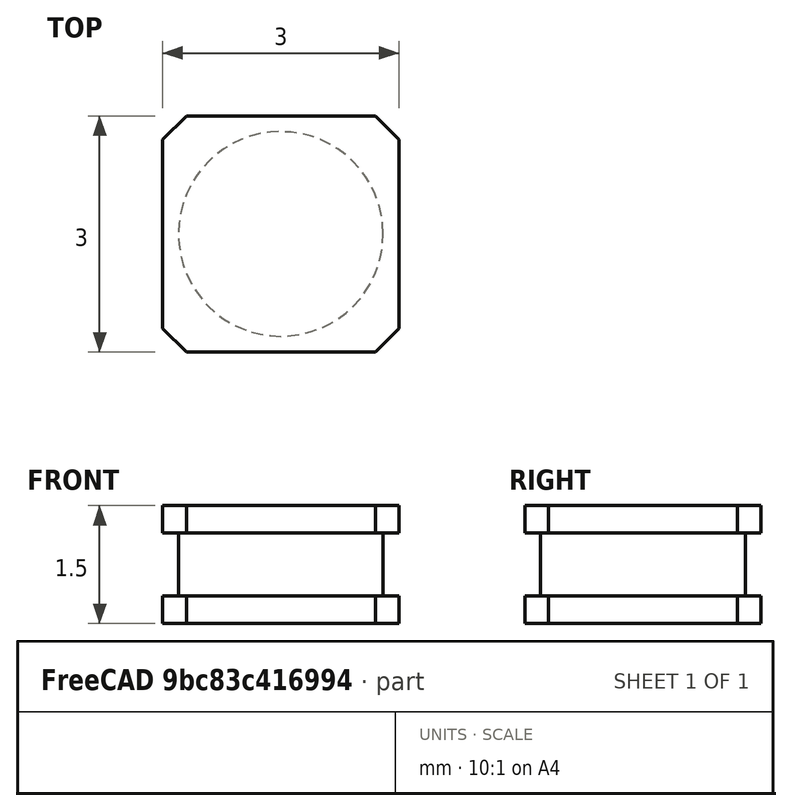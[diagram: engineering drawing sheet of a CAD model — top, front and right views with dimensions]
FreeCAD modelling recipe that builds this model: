
FCSTD DOCUMENT  (FreeCAD 0.19R24366 (Git))
Label: Inductor_shielded_3.0_3.0_1.5
License: All rights reserved
LicenseURL: http://en.wikipedia.org/wiki/All_rights_reserved
objects: Part::Box×2, Part::Chamfer×2, Part::Cylinder×1, Part::MultiFuse×1
note: 6 computed .brp shape members not serialized (recipe doc carries the construction recipe); baked Part::Feature solids carry a one-line shape summary decoded from their .brp

FEATURE [Part::Box] Box  label="Kocka"
  AttacherType = Attacher::AttachEngine3D
  Height = 0.35
  Length = 3
  Width = 3
FEATURE [Part::Chamfer] Chamfer
  Base = -> Box
  Edges = 4 edges r=0.3: [Edge1,Edge3,Edge5,Edge7]
FEATURE [Part::Box] Box001  label="Kocka001"
  AttacherType = Attacher::AttachEngine3D
  Height = 0.35
  Length = 3
  Width = 3
FEATURE [Part::Chamfer] Chamfer001
  Base = -> Box001
  Edges = 4 edges r=0.3: [Edge1,Edge3,Edge5,Edge7]
  Placement = pos=(0,0,1.15) rot=(0,0,1;0rad)
FEATURE [Part::Cylinder] Cylinder  label="Henger"
  Angle = 360
  AttacherType = Attacher::AttachEngine3D
  Height = 1.3
  Placement = pos=(1.5,1.5,0.1) rot=(0,0,1;0rad)
  Radius = 1.3
FEATURE [Part::MultiFuse] Fusion
  Shapes = -> [Chamfer,Chamfer001,Cylinder]
